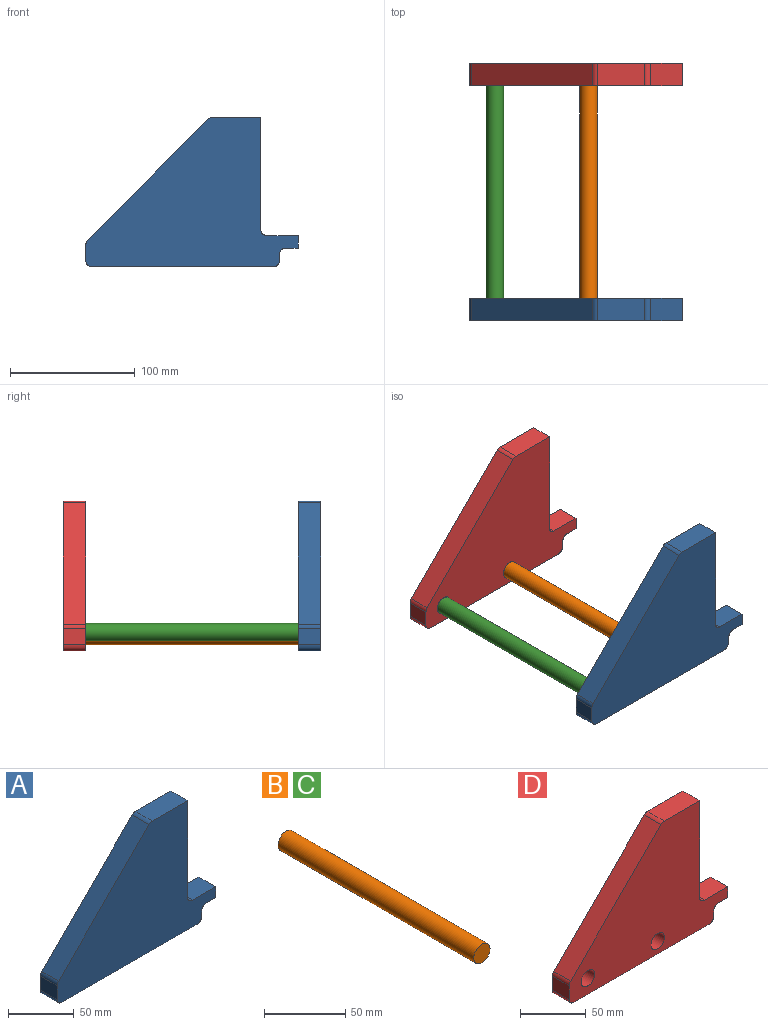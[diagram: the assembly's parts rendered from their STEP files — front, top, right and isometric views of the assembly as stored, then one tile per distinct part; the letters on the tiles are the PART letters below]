
ASSEMBLY  parts=4 mates=7
PART A: 21 faces, bbox 170x18x120 mm
  f0: plane 145x18mm, normal (0,0,-1), area 2610mm2, adj f1,f14,f15,f16
  f1: cylinder r=5mm len=18mm, axis (0,1,0), area 141.4mm2, adj f0,f2,f15,f16
  f2: plane 18x5mm, normal (1,0,0), area 90mm2, adj f1,f3,f15,f16
  f3: cylinder r=5mm len=18mm, axis (0,1,0), area 141.4mm2, adj f2,f4,f15,f16
  f4: plane 18x10mm, normal (0,0,-1), area 180mm2, adj f3,f5,f15,f16
  f5: plane 18x10mm, normal (1,0,0), area 180mm2, adj f4,f6,f15,f16
  f6: plane 25x18mm, normal (0,0,1), area 450mm2, adj f5,f7,f15,f16
  f7: cylinder r=5mm len=18mm, axis (0,1,0), area 141.4mm2, adj f6,f8,f15,f16
  f8: plane 90x18mm, normal (1,0,0), area 1620mm2, adj f7,f9,f15,f16
  f9: plane 37.93x18mm, normal (0,0,1), area 682.7mm2, adj f8,f10,f15,f16
  f10: cylinder r=5mm len=18mm, axis (0,1,0), area 70.7mm2, adj f9,f11,f15,f16
  f11: plane 97.07x97.07mm, normal (-0.71,0,0.71), area 2471mm2, adj f10,f12,f15,f16
  f12: cylinder r=5mm len=18mm, axis (0,1,0), area 70.7mm2, adj f11,f13,f15,f16
  f13: plane 18x12.93mm, normal (-1,0,0), area 232.7mm2, adj f12,f14,f15,f16
  f14: cylinder r=5mm len=18mm, axis (0,1,0), area 141.4mm2, adj f0,f13,f15,f16
  f15: plane 170x120mm, normal (0,-1,0), area 12323.9mm2, adj f0,f1,f2,f3,f4,f5,f6,f7
  f16: plane 170x120mm, normal (0,1,0), area 11993.7mm2, adj f0,f1,f2,f3,f4,f5,f6,f7
  f17: cylinder r=7.25mm len=15mm, axis (0,1,0), area 683.3mm2, adj f16,f18
  f18: plane 14.5x14.5mm, normal (0,1,0), area 165.1mm2, adj f17
  f19: cylinder r=7.25mm len=15mm, axis (0,1,0), area 683.3mm2, adj f16,f20
  f20: plane 14.5x14.5mm, normal (0,1,0), area 165.1mm2, adj f19
PART B: 3 faces, bbox 14x170x14 mm
  f0: cylinder r=7mm len=170mm, axis (0,1,0), area 7477mm2, adj f1,f2
  f1: plane 14x14mm, normal (0,-1,0), area 153.9mm2, adj f0
  f2: plane 14x14mm, normal (0,1,0), area 153.9mm2, adj f0
PART C: same geometry as B
PART D: 21 faces, bbox 170x18x120 mm
  f0: plane 145x18mm, normal (0,0,-1), area 2610mm2, adj f1,f14,f15,f16
  f1: cylinder r=5mm len=18mm, axis (0,1,0), area 141.4mm2, adj f0,f2,f15,f16
  f2: plane 18x5mm, normal (1,0,0), area 90mm2, adj f1,f3,f15,f16
  f3: cylinder r=5mm len=18mm, axis (0,1,0), area 141.4mm2, adj f2,f4,f15,f16
  f4: plane 18x10mm, normal (0,0,-1), area 180mm2, adj f3,f5,f15,f16
  f5: plane 18x10mm, normal (1,0,0), area 180mm2, adj f4,f6,f15,f16
  f6: plane 25x18mm, normal (0,0,1), area 450mm2, adj f5,f7,f15,f16
  f7: cylinder r=5mm len=18mm, axis (0,1,0), area 141.4mm2, adj f6,f8,f15,f16
  f8: plane 90x18mm, normal (1,0,0), area 1620mm2, adj f7,f9,f15,f16
  f9: plane 37.93x18mm, normal (0,0,1), area 682.7mm2, adj f8,f10,f15,f16
  f10: cylinder r=5mm len=18mm, axis (0,1,0), area 70.7mm2, adj f9,f11,f15,f16
  f11: plane 97.07x97.07mm, normal (-0.71,0,0.71), area 2471mm2, adj f10,f12,f15,f16
  f12: cylinder r=5mm len=18mm, axis (0,1,0), area 70.7mm2, adj f11,f13,f15,f16
  f13: plane 18x12.93mm, normal (-1,0,0), area 232.7mm2, adj f12,f14,f15,f16
  f14: cylinder r=5mm len=18mm, axis (0,1,0), area 141.4mm2, adj f0,f13,f15,f16
  f15: plane 170x120mm, normal (0,-1,0), area 11993.7mm2, adj f0,f1,f2,f3,f4,f5,f6,f7
  f16: plane 170x120mm, normal (0,1,0), area 12323.9mm2, adj f0,f1,f2,f3,f4,f5,f6,f7
  f17: cylinder r=7.25mm len=15mm, axis (0,-1,0), area 683.3mm2, adj f15,f18
  f18: plane 14.5x14.5mm, normal (0,-1,0), area 165.1mm2, adj f17
  f19: cylinder r=7.25mm len=15mm, axis (0,-1,0), area 683.3mm2, adj f15,f20
  f20: plane 14.5x14.5mm, normal (0,-1,0), area 165.1mm2, adj f19
PLACE A t=(-39.96,-235.4,7.16)mm
PLACE B t=(-114.96,-65.4,19.16)mm
PLACE C t=(-189.96,-65.4,22.16)mm
PLACE D t=(-39.96,-47.4,7.16)mm fixed
MATE slider B.f0 <-> D.f17  axis (0,1,0) through (-114.96,-150.4,19.16)mm
MATE slider B.f0 <-> A.f19  axis (0,1,0) through (-114.96,-150.4,19.16)mm
MATE planar C.f0 <-> A.f17  axis (0,1,0) through (-189.96,-235.4,22.16)mm
MATE slider C.f0 <-> D.f19  axis (0,1,0) through (-189.96,-150.4,22.16)mm
MATE planar D.f19 <-> C.f0  axis (0,-1,0) through (-189.96,-65.4,22.16)mm
MATE planar B.f0 <-> D.f17  axis (0,1,0) through (-114.96,-65.4,19.16)mm
MATE planar A.f19 <-> B.f0  axis (0,1,0) through (-114.96,-235.4,19.16)mm
